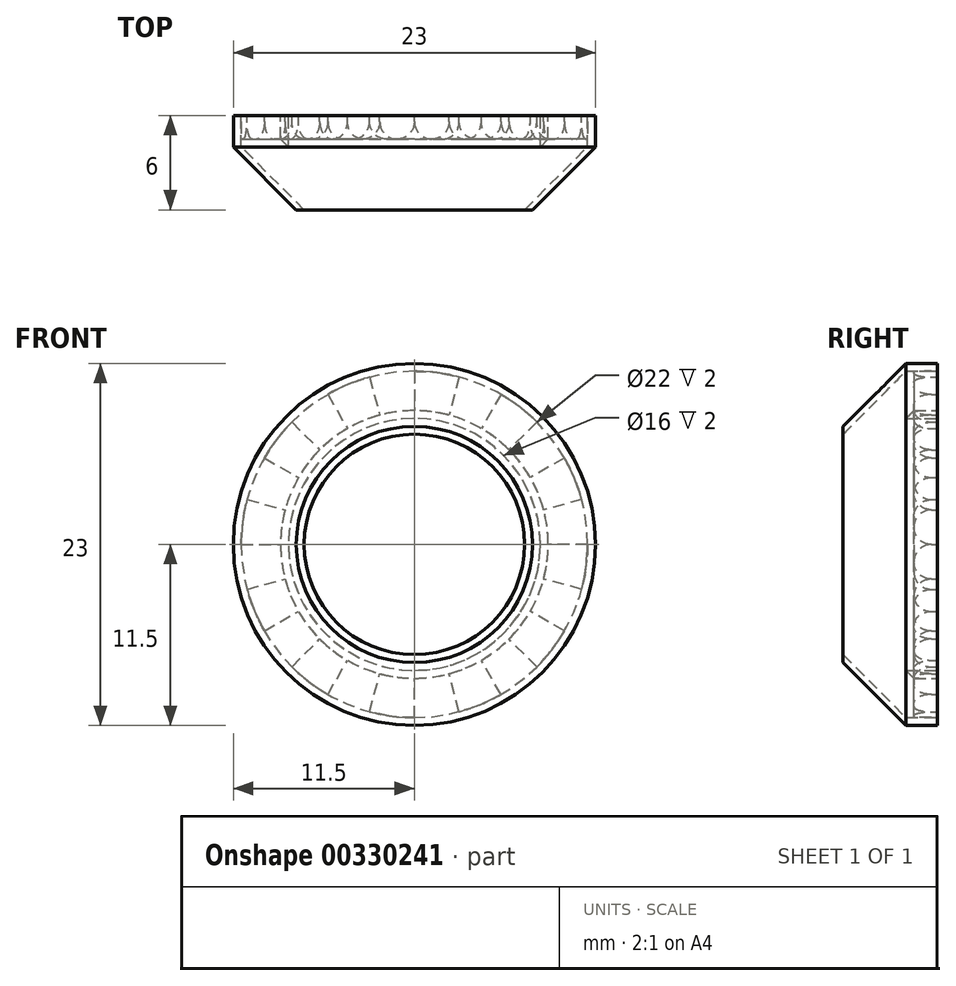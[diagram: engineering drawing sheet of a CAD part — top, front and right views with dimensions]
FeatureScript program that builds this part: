
annotation { "Feature Type Name" : "Feature", "Feature Type Description" : "" }
export const myFeature = defineFeature(function(context is Context, id is Id, definition is map)
    precondition{}
    {
        {
            var Q0;
            Q0=qCreatedBy(makeId("Front.planeOp"),FACE);
            var sketch = newSketch(context, id + "F0", { "sketchPlane" : qUnion([Q0])});
            skCircle(sketch, "E0", {"center": v(0, 0) * mm, "radius": 8.5 * mm});
            skCircle(sketch, "E1", {"center": v(0, 0) * mm, "radius": 8 * mm});
            skLineSegment(sketch, "E2", {"start": v(0, 11) * mm, "end": v(0, 8.5) * mm});
            skLineSegment(sketch, "E3.1.0", {"start": v(-2.85, 10.63) * mm, "end": v(-2.2, 8.21) * mm});
            skLineSegment(sketch, "E3.2.0", {"start": v(-5.5, 9.53) * mm, "end": v(-4.25, 7.36) * mm});
            skLineSegment(sketch, "E3.3.0", {"start": v(-7.78, 7.78) * mm, "end": v(-6.01, 6.01) * mm});
            skLineSegment(sketch, "E3.4.0", {"start": v(-9.53, 5.5) * mm, "end": v(-7.36, 4.25) * mm});
            skLineSegment(sketch, "E3.5.0", {"start": v(-10.63, 2.85) * mm, "end": v(-8.21, 2.2) * mm});
            skLineSegment(sketch, "E3.6.0", {"start": v(-11, 0) * mm, "end": v(-8.5, 0) * mm});
            skLineSegment(sketch, "E3.7.0", {"start": v(-10.63, -2.85) * mm, "end": v(-8.21, -2.2) * mm});
            skLineSegment(sketch, "E3.8.0", {"start": v(-9.53, -5.5) * mm, "end": v(-7.36, -4.25) * mm});
            skLineSegment(sketch, "E3.9.0", {"start": v(-7.78, -7.78) * mm, "end": v(-6.01, -6.01) * mm});
            skLineSegment(sketch, "E3.10.0", {"start": v(-5.5, -9.53) * mm, "end": v(-4.25, -7.36) * mm});
            skLineSegment(sketch, "E3.11.0", {"start": v(-2.85, -10.63) * mm, "end": v(-2.2, -8.21) * mm});
            skLineSegment(sketch, "E3.12.0", {"start": v(0, -11) * mm, "end": v(0, -8.5) * mm});
            skLineSegment(sketch, "E3.13.0", {"start": v(2.85, -10.63) * mm, "end": v(2.2, -8.21) * mm});
            skLineSegment(sketch, "E3.14.0", {"start": v(5.5, -9.53) * mm, "end": v(4.25, -7.36) * mm});
            skLineSegment(sketch, "E3.15.0", {"start": v(7.78, -7.78) * mm, "end": v(6.01, -6.01) * mm});
            skLineSegment(sketch, "E3.16.0", {"start": v(9.53, -5.5) * mm, "end": v(7.36, -4.25) * mm});
            skLineSegment(sketch, "E3.17.0", {"start": v(10.63, -2.85) * mm, "end": v(8.21, -2.2) * mm});
            skLineSegment(sketch, "E3.18.0", {"start": v(11, 0) * mm, "end": v(8.5, 0) * mm});
            skLineSegment(sketch, "E3.19.0", {"start": v(10.63, 2.85) * mm, "end": v(8.21, 2.2) * mm});
            skLineSegment(sketch, "E3.20.0", {"start": v(9.53, 5.5) * mm, "end": v(7.36, 4.25) * mm});
            skLineSegment(sketch, "E3.21.0", {"start": v(7.78, 7.78) * mm, "end": v(6.01, 6.01) * mm});
            skLineSegment(sketch, "E3.22.0", {"start": v(5.5, 9.53) * mm, "end": v(4.25, 7.36) * mm});
            skLineSegment(sketch, "E3.23.0", {"start": v(2.85, 10.63) * mm, "end": v(2.2, 8.21) * mm});
            skArc(sketch, "E4", {"start": v(0, 11) * mm, "mid": v(1.44, 10.9) * mm, "end": v(2.85, 10.63) * mm});
            skArc(sketch, "E5", {"start": v(5.5, 9.53) * mm, "mid": v(6.7, 8.73) * mm, "end": v(7.78, 7.78) * mm});
            skArc(sketch, "E6", {"start": v(9.53, 5.5) * mm, "mid": v(10.16, 4.2) * mm, "end": v(10.63, 2.85) * mm});
            skArc(sketch, "E7", {"start": v(11, 0) * mm, "mid": v(10.9, -1.44) * mm, "end": v(10.63, -2.85) * mm});
            skArc(sketch, "E8", {"start": v(9.53, -5.5) * mm, "mid": v(8.73, -6.7) * mm, "end": v(7.78, -7.78) * mm});
            skArc(sketch, "E9", {"start": v(5.5, -9.53) * mm, "mid": v(4.2, -10.16) * mm, "end": v(2.85, -10.63) * mm});
            skArc(sketch, "E10", {"start": v(0, -11) * mm, "mid": v(-1.44, -10.9) * mm, "end": v(-2.85, -10.63) * mm});
            skArc(sketch, "E11", {"start": v(-5.5, -9.53) * mm, "mid": v(-6.7, -8.73) * mm, "end": v(-7.78, -7.78) * mm});
            skArc(sketch, "E12", {"start": v(-9.53, -5.5) * mm, "mid": v(-10.16, -4.2) * mm, "end": v(-10.63, -2.85) * mm});
            skArc(sketch, "E13", {"start": v(-11, 0) * mm, "mid": v(-10.9, 1.44) * mm, "end": v(-10.63, 2.85) * mm});
            skArc(sketch, "E14", {"start": v(-9.53, 5.5) * mm, "mid": v(-8.73, 6.7) * mm, "end": v(-7.78, 7.78) * mm});
            skArc(sketch, "E15", {"start": v(-5.5, 9.53) * mm, "mid": v(-4.2, 10.16) * mm, "end": v(-2.85, 10.63) * mm});
            skSolve(sketch);
        }
        {
            var Q0;
            Q0 = qSketchRegion(id + "F0", true);
            extrude(context, id + "F1", {"entities" : qUnion([Q0]), "depth" : 1.5 * mm});
        }
        {
            var Q0;
            Q0=makeQuery(id+"F1.opExtrude","CAP_EDGE",EDGE,{"disambiguationData":[OSD([sQuery(id+"F0.wireOp",EDGE,"E3.5.0")])],"isStart":false});
            var Q1;
            Q1=makeQuery(id+"F1.opExtrude","CAP_EDGE",EDGE,{"disambiguationData":[OSD([sQuery(id+"F0.wireOp",EDGE,"E3.6.0")])],"isStart":false});
            var Q2;
            Q2=makeQuery(id+"F1.opExtrude","CAP_EDGE",EDGE,{"disambiguationData":[OSD([sQuery(id+"F0.wireOp",EDGE,"E3.7.0")])],"isStart":false});
            var Q3;
            Q3=makeQuery(id+"F1.opExtrude","CAP_EDGE",EDGE,{"disambiguationData":[OSD([sQuery(id+"F0.wireOp",EDGE,"E3.8.0")])],"isStart":false});
            var Q4;
            Q4=makeQuery(id+"F1.opExtrude","CAP_EDGE",EDGE,{"disambiguationData":[OSD([sQuery(id+"F0.wireOp",EDGE,"E3.9.0")])],"isStart":false});
            var Q5;
            Q5=makeQuery(id+"F1.opExtrude","CAP_EDGE",EDGE,{"disambiguationData":[OSD([sQuery(id+"F0.wireOp",EDGE,"E3.10.0")])],"isStart":false});
            var Q6;
            Q6=makeQuery(id+"F1.opExtrude","CAP_EDGE",EDGE,{"disambiguationData":[OSD([sQuery(id+"F0.wireOp",EDGE,"E3.11.0")])],"isStart":false});
            var Q7;
            Q7=makeQuery(id+"F1.opExtrude","CAP_EDGE",EDGE,{"disambiguationData":[OSD([sQuery(id+"F0.wireOp",EDGE,"E3.12.0")])],"isStart":false});
            var Q8;
            Q8=makeQuery(id+"F1.opExtrude","CAP_EDGE",EDGE,{"disambiguationData":[OSD([sQuery(id+"F0.wireOp",EDGE,"E3.13.0")])],"isStart":false});
            var Q9;
            Q9=makeQuery(id+"F1.opExtrude","CAP_EDGE",EDGE,{"disambiguationData":[OSD([sQuery(id+"F0.wireOp",EDGE,"E3.14.0")])],"isStart":false});
            var Q10;
            Q10=makeQuery(id+"F1.opExtrude","CAP_EDGE",EDGE,{"disambiguationData":[OSD([sQuery(id+"F0.wireOp",EDGE,"E3.15.0")])],"isStart":false});
            var Q11;
            Q11=makeQuery(id+"F1.opExtrude","CAP_EDGE",EDGE,{"disambiguationData":[OSD([sQuery(id+"F0.wireOp",EDGE,"E3.16.0")])],"isStart":false});
            var Q12;
            Q12=makeQuery(id+"F1.opExtrude","CAP_EDGE",EDGE,{"disambiguationData":[OSD([sQuery(id+"F0.wireOp",EDGE,"E3.17.0")])],"isStart":false});
            var Q13;
            Q13=makeQuery(id+"F1.opExtrude","CAP_EDGE",EDGE,{"disambiguationData":[OSD([sQuery(id+"F0.wireOp",EDGE,"E3.18.0")])],"isStart":false});
            var Q14;
            Q14=makeQuery(id+"F1.opExtrude","CAP_EDGE",EDGE,{"disambiguationData":[OSD([sQuery(id+"F0.wireOp",EDGE,"E3.19.0")])],"isStart":false});
            var Q15;
            Q15=makeQuery(id+"F1.opExtrude","CAP_EDGE",EDGE,{"disambiguationData":[OSD([sQuery(id+"F0.wireOp",EDGE,"E3.20.0")])],"isStart":false});
            var Q16;
            Q16=makeQuery(id+"F1.opExtrude","CAP_EDGE",EDGE,{"disambiguationData":[OSD([sQuery(id+"F0.wireOp",EDGE,"E3.21.0")])],"isStart":false});
            var Q17;
            Q17=makeQuery(id+"F1.opExtrude","CAP_EDGE",EDGE,{"disambiguationData":[OSD([sQuery(id+"F0.wireOp",EDGE,"E3.22.0")])],"isStart":false});
            var Q18;
            Q18=makeQuery(id+"F1.opExtrude","CAP_EDGE",EDGE,{"disambiguationData":[OSD([sQuery(id+"F0.wireOp",EDGE,"E3.23.0")])],"isStart":false});
            var Q19;
            Q19=makeQuery(id+"F1.opExtrude","CAP_EDGE",EDGE,{"disambiguationData":[OSD([sQuery(id+"F0.wireOp",EDGE,"E2")])],"isStart":false});
            var Q20;
            Q20=makeQuery(id+"F1.opExtrude","CAP_EDGE",EDGE,{"disambiguationData":[OSD([sQuery(id+"F0.wireOp",EDGE,"E3.1.0")])],"isStart":false});
            var Q21;
            Q21=makeQuery(id+"F1.opExtrude","CAP_EDGE",EDGE,{"disambiguationData":[OSD([sQuery(id+"F0.wireOp",EDGE,"E3.2.0")])],"isStart":false});
            var Q22;
            Q22=makeQuery(id+"F1.opExtrude","CAP_EDGE",EDGE,{"disambiguationData":[OSD([sQuery(id+"F0.wireOp",EDGE,"E3.3.0")])],"isStart":false});
            var Q23;
            Q23=makeQuery(id+"F1.opExtrude","CAP_EDGE",EDGE,{"disambiguationData":[OSD([sQuery(id+"F0.wireOp",EDGE,"E3.4.0")])],"isStart":false});
            fillet(context, id + "F2", {"entities" : qUnion([Q0, Q1, Q2, Q3, Q4, Q5, Q6, Q7, Q8, Q9, Q10, Q11, Q12, Q13, Q14, Q15, Q16, Q17, Q18, Q19, Q20, Q21, Q22, Q23]), "radius" : 1.1 * mm, "tangentPropagation" : true, "allowEdgeOverflow" : false});
        }
        {
            var Q0;
            Q0=qCreatedBy(makeId("Right.planeOp"),FACE);
            var sketch = newSketch(context, id + "F3", { "sketchPlane" : qUnion([Q0])});
            skLineSegment(sketch, "E16", {"start": v(-1.5, 8) * mm, "end": v(-1.5, 8.5) * mm});
            skLineSegment(sketch, "E17", {"start": v(-1.5, 8) * mm, "end": v(-2, 8) * mm});
            skLineSegment(sketch, "E18", {"start": v(-2, 8) * mm, "end": v(-1.5, 8.5) * mm});
            skSolve(sketch);
        }
        {
            var Q0;
            Q0=qCreatedBy(makeId("Right.planeOp"),FACE);
            var sketch = newSketch(context, id + "F4", { "sketchPlane" : qUnion([Q0])});
            skLineSegment(sketch, "E19", {"start": v(0, 11) * mm, "end": v(-2, 11) * mm});
            skLineSegment(sketch, "E20", {"start": v(-2, 11) * mm, "end": v(-6, 7) * mm});
            skLineSegment(sketch, "E21", {"start": v(0, 11) * mm, "end": v(0, 11.5) * mm});
            skLineSegment(sketch, "E22", {"start": v(0, 11.5) * mm, "end": v(-2, 11.5) * mm});
            skLineSegment(sketch, "E23", {"start": v(-6, 7) * mm, "end": v(-6, 7.5) * mm});
            skLineSegment(sketch, "E24", {"start": v(-6, 7.5) * mm, "end": v(-2, 11.5) * mm});
            skSolve(sketch);
        }
        {
            var Q0;
            Q0 = qSketchRegion(id + "F4", true);
            var Q1;
            Q1=makeQuery(id+"F1.opExtrude","CAP_EDGE",EDGE,{"disambiguationData":[OSD([sQuery(id+"F0.wireOp",EDGE,"E1")])],"isStart":false});
            revolve(context, id + "F5", {"entities" : qUnion([Q0]), "axis" : qUnion([Q1]), "revolveType" : RevolveType.FULL});
        }
        {
            var Q0;
            Q0 = qSketchRegion(id + "F3", true);
            var Q1;
            Q1=makeQuery(id+"F1.opExtrude","CAP_EDGE",EDGE,{"disambiguationData":[OSD([sQuery(id+"F0.wireOp",EDGE,"E1")])],"isStart":false});
            revolve(context, id + "F6", {"operationType" : NewBodyOperationType.ADD, "entities" : qUnion([Q0]), "axis" : qUnion([Q1]), "revolveType" : RevolveType.FULL});
        }
    });
